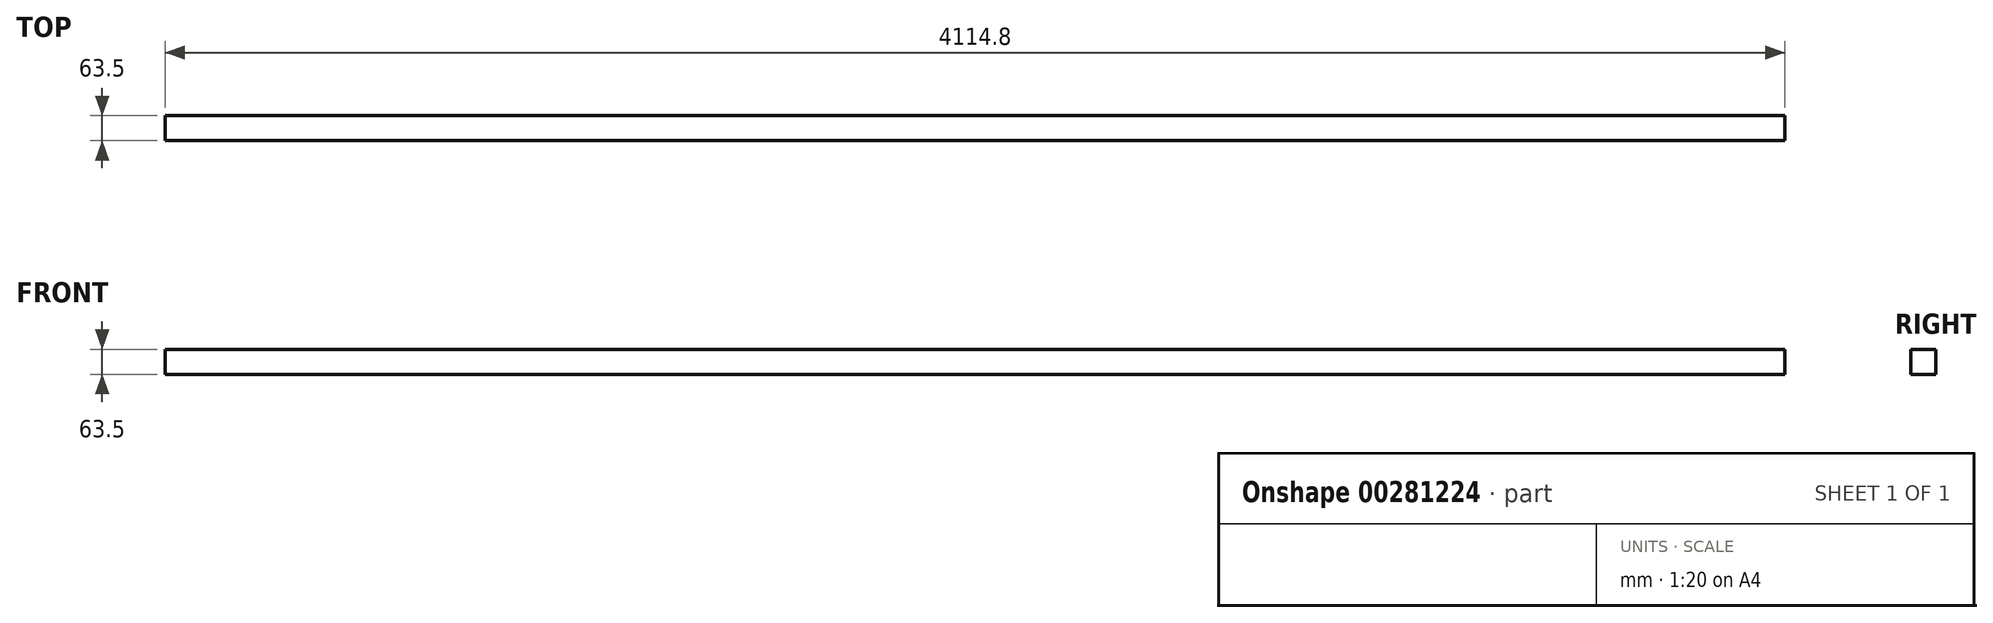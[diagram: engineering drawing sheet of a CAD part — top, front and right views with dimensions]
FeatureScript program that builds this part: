
annotation { "Feature Type Name" : "Feature", "Feature Type Description" : "" }
export const myFeature = defineFeature(function(context is Context, id is Id, definition is map)
    precondition{}
    {
        {
            var Q0;
            Q0=qCreatedBy(makeId("Right.planeOp"),FACE);
            var sketch = newSketch(context, id + "F0", { "sketchPlane" : qUnion([Q0])});
            skLineSegment(sketch, "E0.bottom", {"start": v(-31.75, 31.75) * mm, "end": v(31.75, 31.75) * mm});
            skLineSegment(sketch, "E0.top", {"start": v(-31.75, -31.75) * mm, "end": v(31.75, -31.75) * mm});
            skLineSegment(sketch, "E0.left", {"start": v(-31.75, 31.75) * mm, "end": v(-31.75, -31.75) * mm});
            skLineSegment(sketch, "E0.right", {"start": v(31.75, 31.75) * mm, "end": v(31.75, -31.75) * mm});
            skPoint(sketch, "E0.middle", {"position": v(0, 0) * mm});
            skSolve(sketch);
        }
        {
            var Q0;
            Q0=makeQuery(id+"F0.imprint","IMPRINT",FACE,{"disambiguationData":[TD([[makeQuery(id+"F0.imprint","IMPRINT",EDGE,{"derivedFrom":sQuery(id+"F0.wireOp",EDGE,"E0.bottom")}),-1.0]])]});
            extrude(context, id + "F1", {"entities" : qUnion([Q0]), "endBound" : BoundingType.SYMMETRIC, "depth" : 4114.8 * mm});
        }
    });
